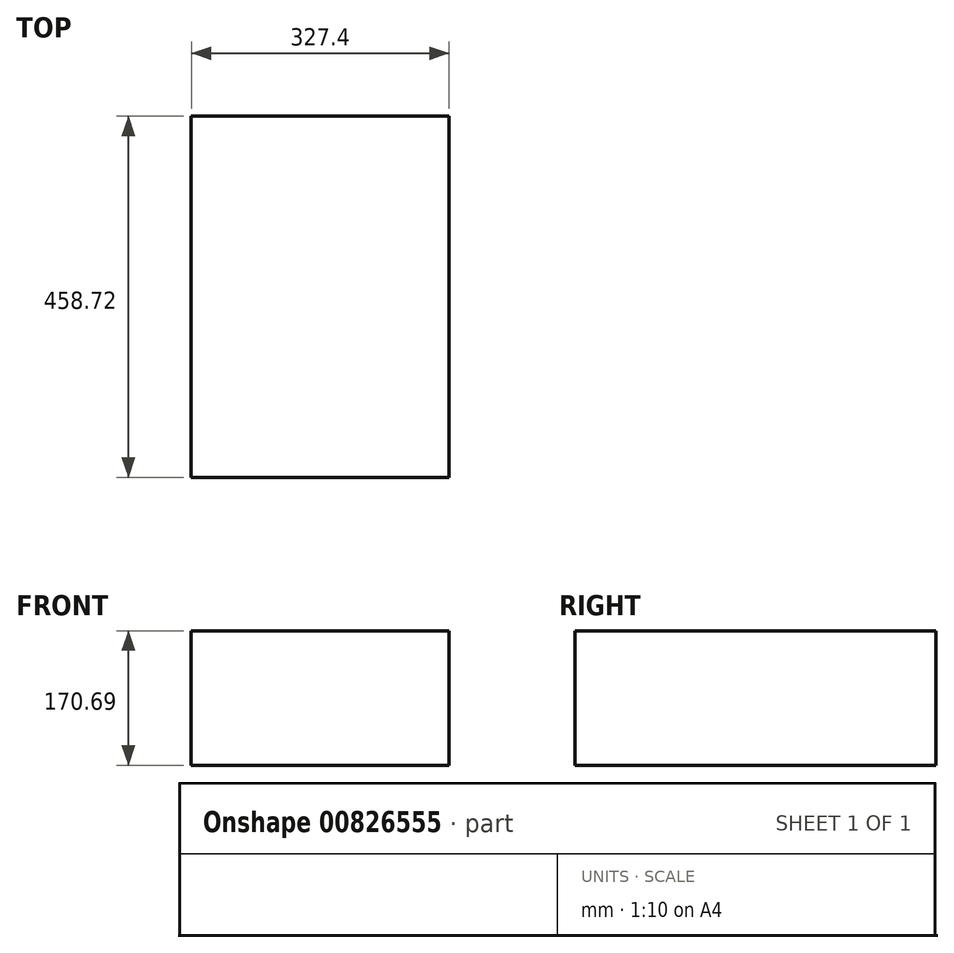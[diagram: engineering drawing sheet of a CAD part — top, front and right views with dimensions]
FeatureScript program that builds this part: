
annotation { "Feature Type Name" : "Feature", "Feature Type Description" : "" }
export const myFeature = defineFeature(function(context is Context, id is Id, definition is map)
    precondition{}
    {
        {
            var Q0;
            Q0=qCreatedBy(makeId("Top.planeOp"),FACE);
            var sketch = newSketch(context, id + "F0", { "sketchPlane" : qUnion([Q0])});
            skLineSegment(sketch, "E0.bottom", {"start": v(163.7, 229.36) * mm, "end": v(-163.7, 229.36) * mm});
            skLineSegment(sketch, "E0.top", {"start": v(163.7, -229.36) * mm, "end": v(-163.7, -229.36) * mm});
            skLineSegment(sketch, "E0.left", {"start": v(163.7, 229.36) * mm, "end": v(163.7, -229.36) * mm});
            skLineSegment(sketch, "E0.right", {"start": v(-163.7, 229.36) * mm, "end": v(-163.7, -229.36) * mm});
            skPoint(sketch, "E0.middle", {"position": v(0, 0) * mm});
            skSolve(sketch);
        }
        {
            var Q0;
            Q0 = qSketchRegion(id + "F0", true);
            extrude(context, id + "F1", {"entities" : qUnion([Q0]), "depth" : 170.7 * mm, "offsetDistance" : 25.4 * mm});
        }
    });
